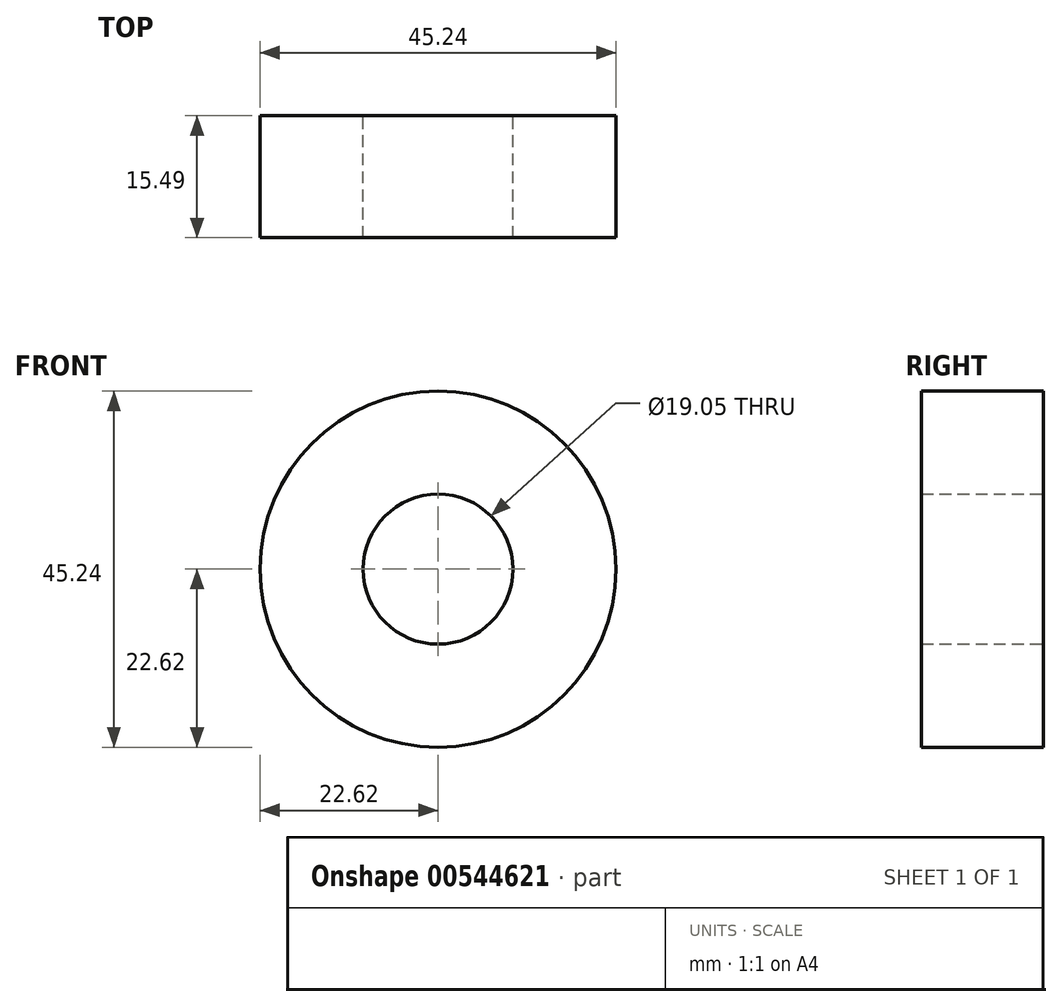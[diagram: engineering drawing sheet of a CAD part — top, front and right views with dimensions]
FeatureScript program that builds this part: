
annotation { "Feature Type Name" : "Feature", "Feature Type Description" : "" }
export const myFeature = defineFeature(function(context is Context, id is Id, definition is map)
    precondition{}
    {
        {
            var Q0;
            Q0=qCreatedBy(makeId("Front.planeOp"),FACE);
            var sketch = newSketch(context, id + "F0", { "sketchPlane" : qUnion([Q0])});
            skCircle(sketch, "E0", {"center": v(0, 0) * mm, "radius": 9.53 * mm});
            skCircle(sketch, "E1", {"center": v(0, 0) * mm, "radius": 22.62 * mm});
            skSolve(sketch);
        }
        {
            var Q0;
            Q0 = qSketchRegion(id + "F0", true);
            extrude(context, id + "F1", {"entities" : qUnion([Q0]), "depth" : 15.5 * mm, "offsetDistance" : 25.4 * mm});
        }
    });
